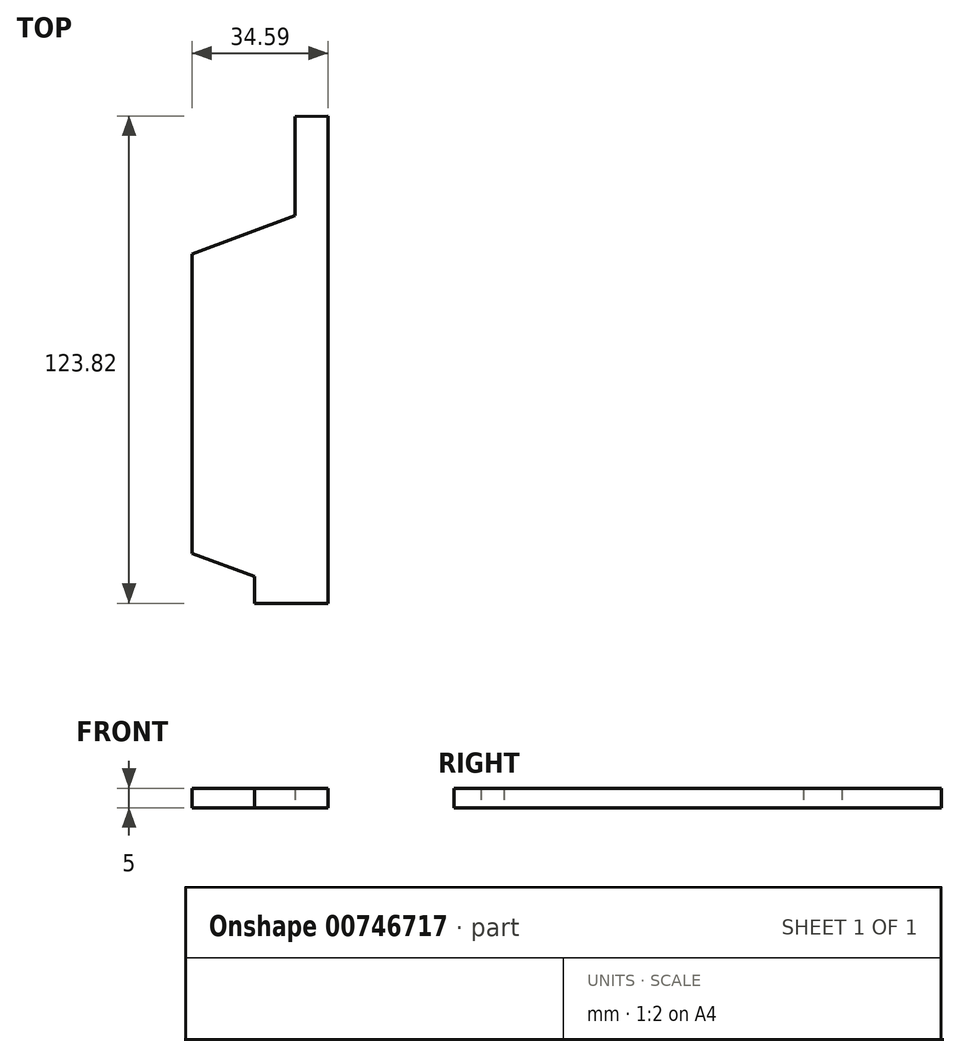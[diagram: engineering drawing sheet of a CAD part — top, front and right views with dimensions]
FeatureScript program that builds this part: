
annotation { "Feature Type Name" : "Feature", "Feature Type Description" : "" }
export const myFeature = defineFeature(function(context is Context, id is Id, definition is map)
    precondition{}
    {
        {
            var Q0;
            Q0=qCreatedBy(makeId("Top.planeOp"),FACE);
            var sketch = newSketch(context, id + "F0", { "sketchPlane" : qUnion([Q0])});
            skLineSegment(sketch, "E0", {"start": v(-8.38, 46.56) * mm, "end": v(-8.38, 21.33) * mm});
            skLineSegment(sketch, "E1", {"start": v(-8.38, 21.33) * mm, "end": v(-34.6, 11.56) * mm});
            skLineSegment(sketch, "E2", {"start": v(-34.6, 11.56) * mm, "end": v(-34.6, -64.46) * mm});
            skLineSegment(sketch, "E3", {"start": v(-34.6, -64.46) * mm, "end": v(-18.64, -70.32) * mm});
            skLineSegment(sketch, "E4", {"start": v(-18.64, -70.32) * mm, "end": v(-18.64, -77.16) * mm});
            skLineSegment(sketch, "E5", {"start": v(-18.64, -77.16) * mm, "end": v(0, -77.16) * mm});
            skLineSegment(sketch, "E6", {"start": v(0, -77.16) * mm, "end": v(0, 46.66) * mm});
            skLineSegment(sketch, "E7", {"start": v(0, 46.66) * mm, "end": v(-8.38, 46.56) * mm});
            skSolve(sketch);
        }
        {
            var Q0;
            Q0=makeQuery(id+"F0.imprint","IMPRINT",FACE,{"disambiguationData":[TD([[makeQuery(id+"F0.imprint","IMPRINT",EDGE,{"derivedFrom":sQuery(id+"F0.wireOp",EDGE,"E0")}),1.0]])]});
            var Q1;
            Q1=makeQuery(id+"FyTyko17EGR5IDr_0.1.F0.imprint","IMPRINT",FACE,{"disambiguationData":[TD([[makeQuery(id+"FyTyko17EGR5IDr_0.1.F0.imprint","IMPRINT",EDGE,{"derivedFrom":sQuery(id+"FyTyko17EGR5IDr_0.1.F0.wireOp",EDGE,"E0")}),1.0]])]});
            extrude(context, id + "F1", {"entities" : qUnion([Q0, Q1]), "depth" : 5 * mm, "offsetDistance" : 25.4 * mm});
        }
    });
